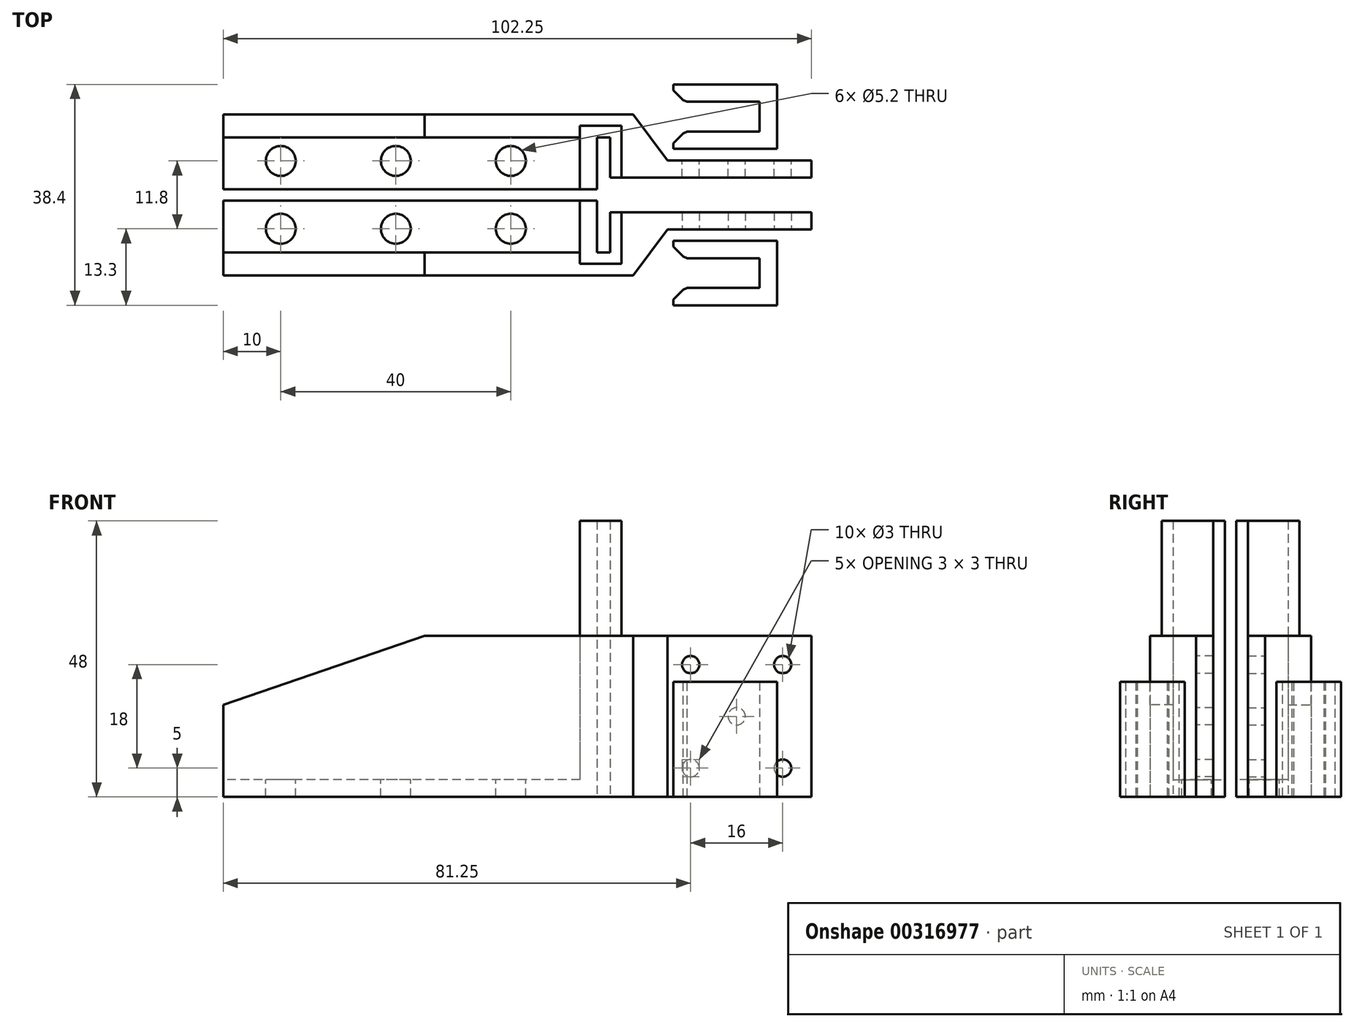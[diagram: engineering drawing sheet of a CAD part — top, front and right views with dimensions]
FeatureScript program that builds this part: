
annotation { "Feature Type Name" : "Feature", "Feature Type Description" : "" }
export const myFeature = defineFeature(function(context is Context, id is Id, definition is map)
    precondition{}
    {
        {
            var Q0;
            Q0=qCreatedBy(makeId("Top.planeOp"),FACE);
            var sketch = newSketch(context, id + "F0", { "sketchPlane" : qUnion([Q0])});
            skLineSegment(sketch, "E0", {"start": v(0, -7) * mm, "end": v(0, 0) * mm});
            skLineSegment(sketch, "E1", {"start": v(0, 0) * mm, "end": v(35, 0) * mm});
            skLineSegment(sketch, "E2", {"start": v(35, 0) * mm, "end": v(35, -3) * mm});
            skLineSegment(sketch, "E3", {"start": v(35, -3) * mm, "end": v(10, -3) * mm});
            skLineSegment(sketch, "E4", {"start": v(10, -3) * mm, "end": v(4, -11) * mm});
            skLineSegment(sketch, "E5", {"start": v(4, -11) * mm, "end": v(-2.25, -11) * mm});
            skLineSegment(sketch, "E6", {"start": v(-2.25, -11) * mm, "end": v(-67.25, -11) * mm});
            skLineSegment(sketch, "E7", {"start": v(-67.25, -11) * mm, "end": v(-67.25, 2) * mm});
            skLineSegment(sketch, "E8", {"start": v(-2.25, 2) * mm, "end": v(-2.25, -7) * mm});
            skLineSegment(sketch, "E9", {"start": v(-2.25, -7) * mm, "end": v(0, -7) * mm});
            skLineSegment(sketch, "E10", {"start": v(-67.25, 2) * mm, "end": v(-2.25, 2) * mm});
            skPoint(sketch, "E11.start.orphan", {"position": v(-67.25, 0) * mm});
            skPoint(sketch, "E12.orphan", {"position": v(-2.25, -1) * mm});
            skSolve(sketch);
        }
        {
            var Q0;
            Q0 = qSketchRegion(id + "F0", true);
            extrude(context, id + "F1", {"entities" : qUnion([Q0]), "depth" : 3 * mm});
        }
        {
            var Q0;
            Q0=makeQuery(id+"F1.opExtrude","CAP_FACE",FACE,{"disambiguationData":[OSD([sQuery(id+"F0.wireOp",EDGE,"E0"),sQuery(id+"F0.wireOp",EDGE,"E1"),sQuery(id+"F0.wireOp",EDGE,"E2"),sQuery(id+"F0.wireOp",EDGE,"E3"),sQuery(id+"F0.wireOp",EDGE,"E4"),sQuery(id+"F0.wireOp",EDGE,"E5"),sQuery(id+"F0.wireOp",EDGE,"E6"),sQuery(id+"F0.wireOp",EDGE,"E7"),sQuery(id+"F0.wireOp",EDGE,"E8"),sQuery(id+"F0.wireOp",EDGE,"E9"),sQuery(id+"F0.wireOp",EDGE,"E10")])],"isStart":false});
            var sketch = newSketch(context, id + "F2", { "sketchPlane" : qUnion([Q0])});
            skLineSegment(sketch, "E13", {"start": v(0, 0) * mm, "end": v(35, 0) * mm});
            skLineSegment(sketch, "E14", {"start": v(35, 0) * mm, "end": v(35, -3) * mm});
            skLineSegment(sketch, "E15", {"start": v(35, -3) * mm, "end": v(10, -3) * mm});
            skLineSegment(sketch, "E16", {"start": v(10, -3) * mm, "end": v(4, -11) * mm});
            skLineSegment(sketch, "E17", {"start": v(4, -11) * mm, "end": v(-67.25, -11) * mm});
            skLineSegment(sketch, "E18", {"start": v(0, 0) * mm, "end": v(0, -7) * mm});
            skLineSegment(sketch, "E19", {"start": v(0, -7) * mm, "end": v(-2.25, -7) * mm});
            skLineSegment(sketch, "E20", {"start": v(-67.25, -7) * mm, "end": v(-67.25, -11) * mm});
            skLineSegment(sketch, "E21", {"start": v(-2.25, -7) * mm, "end": v(-2.25, 2) * mm});
            skLineSegment(sketch, "E22", {"start": v(-2.25, 2) * mm, "end": v(-5.25, 2) * mm});
            skLineSegment(sketch, "E23", {"start": v(-5.25, 2) * mm, "end": v(-5.25, -7) * mm});
            skLineSegment(sketch, "E24.trimOffspring", {"start": v(-5.25, -7) * mm, "end": v(-67.25, -7) * mm});
            skSolve(sketch);
        }
        {
            var Q0;
            Q0 = qSketchRegion(id + "F2", true);
            extrude(context, id + "F3", {"entities" : qUnion([Q0]), "operationType" : NewBodyOperationType.ADD, "depth" : 25 * mm});
        }
        {
            var Q0;
            Q0=qCreatedBy(makeId("Front.planeOp"),FACE);
            cPlane(context, id + "F4", {"entities" : qUnion([Q0]), "cplaneType" : CPlaneType.OFFSET, "offset" : 3 * mm, "oppositeDirection" : true, "width" : 150 * mm, "height" : 150 * mm});
        }
        {
            var Q0;
            Q0=makeQuery(id+"F1.opExtrude","CAP_FACE",FACE,{"disambiguationData":[OSD([sQuery(id+"F0.wireOp",EDGE,"E0"),sQuery(id+"F0.wireOp",EDGE,"E1"),sQuery(id+"F0.wireOp",EDGE,"E2"),sQuery(id+"F0.wireOp",EDGE,"E3"),sQuery(id+"F0.wireOp",EDGE,"E4"),sQuery(id+"F0.wireOp",EDGE,"E5"),sQuery(id+"F0.wireOp",EDGE,"E6"),sQuery(id+"F0.wireOp",EDGE,"E7"),sQuery(id+"F0.wireOp",EDGE,"E8"),sQuery(id+"F0.wireOp",EDGE,"E9"),sQuery(id+"F0.wireOp",EDGE,"E10")])],"isStart":false});
            var sketch = newSketch(context, id + "F5", { "sketchPlane" : qUnion([Q0])});
            skCircle(sketch, "E25", {"center": v(-17.25, -2.9) * mm, "radius": 2.6 * mm});
            skCircle(sketch, "E26", {"center": v(-37.25, -2.9) * mm, "radius": 2.6 * mm});
            skCircle(sketch, "E27", {"center": v(-57.25, -2.9) * mm, "radius": 2.6 * mm});
            skSolve(sketch);
        }
        {
            var Q0;
            Q0 = qSketchRegion(id + "F5", true);
            extrude(context, id + "F6", {"entities" : qUnion([Q0]), "operationType" : NewBodyOperationType.REMOVE, "endBound" : BoundingType.UP_TO_NEXT, "oppositeDirection" : true, "depth" : 25 * mm});
        }
        {
            var Q0;
            Q0=makeQuery(id+"F3.boolean.opBoolean","MERGE",FACE,{"derivedFrom":[makeQuery(id+"F1.opExtrude","SWEPT_FACE",FACE,{"disambiguationData":[OSD([sQuery(id+"F0.wireOp",EDGE,"E3")])]}),makeQuery(id+"F3.opExtrude","SWEPT_FACE",FACE,{"disambiguationData":[OSD([sQuery(id+"F2.wireOp",EDGE,"E15")])]})]});
            var sketch = newSketch(context, id + "F7", { "sketchPlane" : qUnion([Q0])});
            skCircle(sketch, "E28", {"center": v(30, 5) * mm, "radius": 1.5 * mm});
            skCircle(sketch, "E29", {"center": v(14, 5) * mm, "radius": 1.5 * mm});
            skCircle(sketch, "E30", {"center": v(14, 23) * mm, "radius": 1.5 * mm});
            skCircle(sketch, "E31", {"center": v(30, 23) * mm, "radius": 1.5 * mm});
            skLineSegment(sketch, "E32", {"start": v(30, 23) * mm, "end": v(14, 5) * mm, "construction": true});
            skCircle(sketch, "E33", {"center": v(22, 14) * mm, "radius": 1.5 * mm});
            skSolve(sketch);
        }
        {
            var Q0;
            Q0 = qSketchRegion(id + "F7", true);
            extrude(context, id + "F8", {"entities" : qUnion([Q0]), "operationType" : NewBodyOperationType.REMOVE, "endBound" : BoundingType.UP_TO_NEXT, "oppositeDirection" : true, "depth" : 25 * mm});
        }
        {
            var Q0;
            Q0=makeQuery(id+"F3.boolean.opBoolean","MERGE",FACE,{"derivedFrom":[makeQuery(id+"F1.opExtrude","SWEPT_FACE",FACE,{"disambiguationData":[OSD([sQuery(id+"F0.wireOp",EDGE,"E5"),sQuery(id+"F0.wireOp",EDGE,"E6")])]}),makeQuery(id+"F3.opExtrude","SWEPT_FACE",FACE,{"disambiguationData":[OSD([sQuery(id+"F2.wireOp",EDGE,"E17")])]})]});
            var sketch = newSketch(context, id + "F9", { "sketchPlane" : qUnion([Q0])});
            skLineSegment(sketch, "E34", {"start": v(-67.25, 16) * mm, "end": v(-32.25, 28) * mm});
            skLineSegment(sketch, "E35", {"start": v(-32.25, 28) * mm, "end": v(-67.25, 28) * mm});
            skLineSegment(sketch, "E36", {"start": v(-67.25, 28) * mm, "end": v(-67.25, 16) * mm});
            skSolve(sketch);
        }
        {
            var Q0;
            Q0 = qSketchRegion(id + "F9", true);
            extrude(context, id + "F10", {"entities" : qUnion([Q0]), "operationType" : NewBodyOperationType.REMOVE, "endBound" : BoundingType.UP_TO_NEXT, "oppositeDirection" : true, "depth" : 25 * mm});
        }
        {
            var Q0;
            Q0=makeQuery(id+"F3.opExtrude","CAP_FACE",FACE,{"disambiguationData":[OSD([sQuery(id+"F2.wireOp",EDGE,"E13"),sQuery(id+"F2.wireOp",EDGE,"E14"),sQuery(id+"F2.wireOp",EDGE,"E15"),sQuery(id+"F2.wireOp",EDGE,"E16"),sQuery(id+"F2.wireOp",EDGE,"E17"),sQuery(id+"F2.wireOp",EDGE,"E18"),sQuery(id+"F2.wireOp",EDGE,"E19"),sQuery(id+"F2.wireOp",EDGE,"E20"),sQuery(id+"F2.wireOp",EDGE,"E21"),sQuery(id+"F2.wireOp",EDGE,"E22"),sQuery(id+"F2.wireOp",EDGE,"E23"),sQuery(id+"F2.wireOp",EDGE,"E24.trimOffspring")])],"isStart":false});
            var sketch = newSketch(context, id + "F11", { "sketchPlane" : qUnion([Q0])});
            skLineSegment(sketch, "E37", {"start": v(-2.25, 2) * mm, "end": v(-2.25, -7) * mm});
            skLineSegment(sketch, "E38", {"start": v(-2.25, -7) * mm, "end": v(0, -7) * mm});
            skLineSegment(sketch, "E39", {"start": v(0, -7) * mm, "end": v(0, 0) * mm});
            skLineSegment(sketch, "E40", {"start": v(0, 0) * mm, "end": v(2, 0) * mm});
            skLineSegment(sketch, "E41", {"start": v(2, 0) * mm, "end": v(2, -9) * mm});
            skLineSegment(sketch, "E42", {"start": v(2, -9) * mm, "end": v(-5.25, -9) * mm});
            skLineSegment(sketch, "E43", {"start": v(-5.25, -9) * mm, "end": v(-5.25, 2) * mm});
            skLineSegment(sketch, "E44", {"start": v(-5.25, 2) * mm, "end": v(-2.25, 2) * mm});
            skSolve(sketch);
        }
        {
            var Q0;
            Q0 = qSketchRegion(id + "F11", true);
            extrude(context, id + "F12", {"entities" : qUnion([Q0]), "operationType" : NewBodyOperationType.ADD, "depth" : 20 * mm});
        }
        {
            var Q0;
            Q0=makeQuery(id+"F1.opExtrude","SWEPT_BODY",BODY,{"disambiguationData":[OSD([sQuery(id+"F0.wireOp",EDGE,"E0"),sQuery(id+"F0.wireOp",EDGE,"E1"),sQuery(id+"F0.wireOp",EDGE,"E2"),sQuery(id+"F0.wireOp",EDGE,"E3"),sQuery(id+"F0.wireOp",EDGE,"E4"),sQuery(id+"F0.wireOp",EDGE,"E5"),sQuery(id+"F0.wireOp",EDGE,"E6"),sQuery(id+"F0.wireOp",EDGE,"E7"),sQuery(id+"F0.wireOp",EDGE,"E8"),sQuery(id+"F0.wireOp",EDGE,"E9"),sQuery(id+"F0.wireOp",EDGE,"E10")])]});
            var Q1;
            Q1=qCreatedBy(id+"F4.planeOp",FACE);
            mirror(context, id + "F13", {"entities" : qUnion([Q0]), "mirrorPlane" : qUnion([Q1])});
        }
        {
            var Q0;
            Q0=qCreatedBy(makeId("Top.planeOp"),FACE);
            var sketch = newSketch(context, id + "F14", { "sketchPlane" : qUnion([Q0])});
            skLineSegment(sketch, "E45", {"start": v(11, 14) * mm, "end": v(11, 11) * mm});
            skLineSegment(sketch, "E46", {"start": v(11, 11) * mm, "end": v(29, 11) * mm});
            skLineSegment(sketch, "E47", {"start": v(29, 11) * mm, "end": v(29, 22.2) * mm});
            skLineSegment(sketch, "E48", {"start": v(29, 22.2) * mm, "end": v(11, 22.2) * mm});
            skLineSegment(sketch, "E49", {"start": v(11, 22.2) * mm, "end": v(11, 19.2) * mm});
            skLineSegment(sketch, "E50", {"start": v(11, 19.2) * mm, "end": v(26, 19.2) * mm});
            skLineSegment(sketch, "E51", {"start": v(26, 19.2) * mm, "end": v(26, 14) * mm});
            skLineSegment(sketch, "E52", {"start": v(26, 14) * mm, "end": v(11, 14) * mm});
            skSolve(sketch);
        }
        {
            var Q0;
            Q0 = qSketchRegion(id + "F14", true);
            extrude(context, id + "F15", {"entities" : qUnion([Q0]), "depth" : 20 * mm});
        }
        {
            var Q0;
            Q0=makeQuery(id+"F15.opExtrude","SWEPT_EDGE",EDGE,{"disambiguationData":[OSD([sQuery(id+"F14.wireOp",EDGE,"E49"),sQuery(id+"F14.wireOp",EDGE,"E50")])]});
            var Q1;
            Q1=makeQuery(id+"F15.opExtrude","SWEPT_EDGE",EDGE,{"disambiguationData":[OSD([sQuery(id+"F14.wireOp",EDGE,"E45"),sQuery(id+"F14.wireOp",EDGE,"E52")])]});
            chamfer(context, id + "F16", {"entities" : qUnion([Q0, Q1]), "width" : 2 * mm, "tangentPropagation" : true});
        }
        {
            var Q0;
            {var subQ0=sQuery(id+"F14.wireOp",EDGE,"E52");Q0=makeQuery(id+"F16.opChamfer","BLEND_EDGE",EDGE,{"blendedFrom":[makeQuery(id+"F15.opExtrude","SWEPT_EDGE",EDGE,{"disambiguationData":[OSD([sQuery(id+"F14.wireOp",EDGE,"E45"),subQ0])]}),makeQuery(id+"F15.opExtrude","SWEPT_FACE",FACE,{"disambiguationData":[OSD([subQ0])]})],"blendedInto":[makeQuery(id+"F15.opExtrude","SWEPT_FACE",FACE,{"disambiguationData":[OSD([subQ0])]})]});}
            var Q1;
            {var subQ0=sQuery(id+"F14.wireOp",EDGE,"E50");Q1=makeQuery(id+"F16.opChamfer","BLEND_EDGE",EDGE,{"blendedFrom":[makeQuery(id+"F15.opExtrude","SWEPT_EDGE",EDGE,{"disambiguationData":[OSD([sQuery(id+"F14.wireOp",EDGE,"E49"),subQ0])]}),makeQuery(id+"F15.opExtrude","SWEPT_FACE",FACE,{"disambiguationData":[OSD([subQ0])]})],"blendedInto":[makeQuery(id+"F15.opExtrude","SWEPT_FACE",FACE,{"disambiguationData":[OSD([subQ0])]})]});}
            chamfer(context, id + "F17", {"entities" : qUnion([Q0, Q1]), "width" : 1 * mm, "tangentPropagation" : true});
        }
        {
            var Q0;
            Q0=makeQuery(id+"F15.opExtrude","SWEPT_BODY",BODY,{"disambiguationData":[OSD([sQuery(id+"F14.wireOp",EDGE,"E45"),sQuery(id+"F14.wireOp",EDGE,"E46"),sQuery(id+"F14.wireOp",EDGE,"E47"),sQuery(id+"F14.wireOp",EDGE,"E48"),sQuery(id+"F14.wireOp",EDGE,"E49"),sQuery(id+"F14.wireOp",EDGE,"E50"),sQuery(id+"F14.wireOp",EDGE,"E51"),sQuery(id+"F14.wireOp",EDGE,"E52")])]});
            var Q1;
            Q1=qCreatedBy(id+"F4.planeOp",FACE);
            mirror(context, id + "F18", {"entities" : qUnion([Q0]), "mirrorPlane" : qUnion([Q1])});
        }
    });
